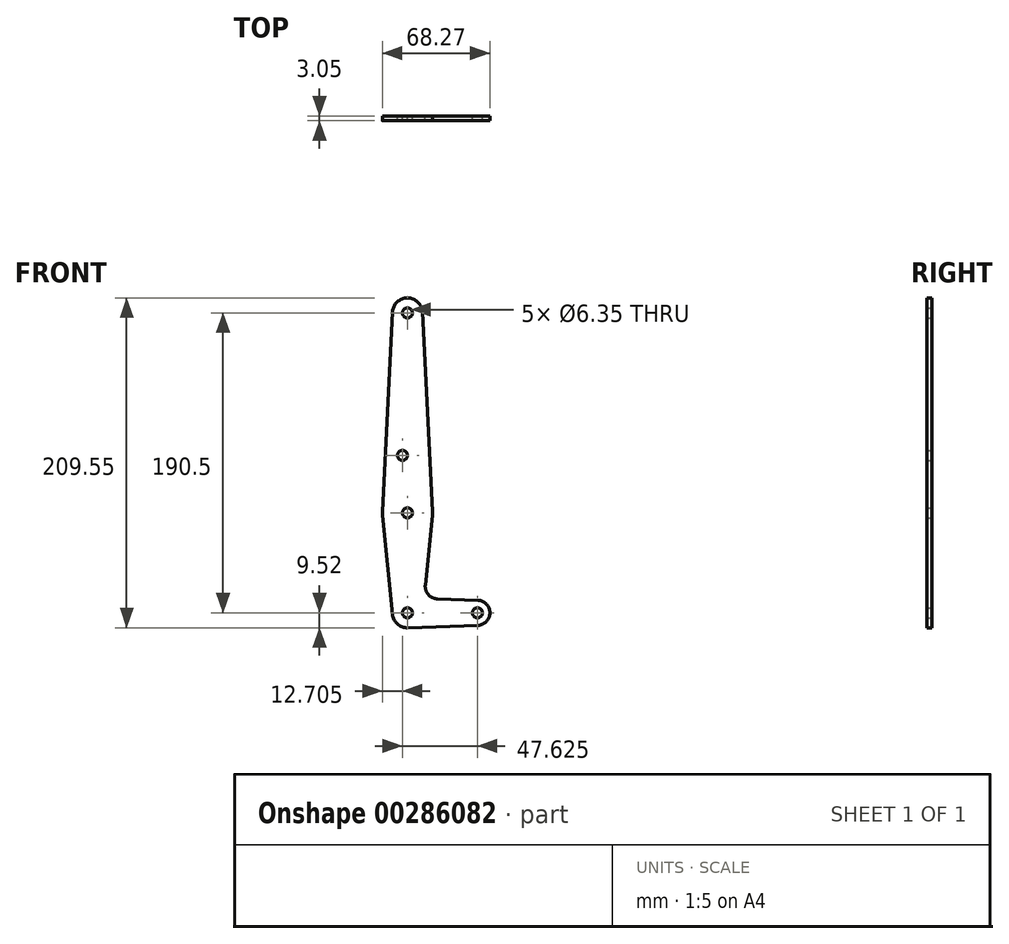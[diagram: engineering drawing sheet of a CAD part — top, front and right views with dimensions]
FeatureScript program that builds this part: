
annotation { "Feature Type Name" : "Feature", "Feature Type Description" : "" }
export const myFeature = defineFeature(function(context is Context, id is Id, definition is map)
    precondition{}
    {
        {
            var Q0;
            Q0=qCreatedBy(makeId("Front.planeOp"),FACE);
            var sketch = newSketch(context, id + "F0", { "sketchPlane" : qUnion([Q0])});
            skCircle(sketch, "E0", {"center": v(0, 0) * mm, "radius": 9.53 * mm});
            skCircle(sketch, "E1", {"center": v(0, 63.5) * mm, "radius": 15.88 * mm});
            skCircle(sketch, "E2", {"center": v(0, 190.5) * mm, "radius": 9.53 * mm});
            skLineSegment(sketch, "E3", {"start": v(0, 0) * mm, "end": v(44.45, 0) * mm, "construction": true});
            skCircle(sketch, "E4", {"center": v(44.45, 0) * mm, "radius": 7.94 * mm});
            skLineSegment(sketch, "E5", {"start": v(0, 190.5) * mm, "end": v(0, 0) * mm, "construction": true});
            skLineSegment(sketch, "E6", {"start": v(9.51, 190.98) * mm, "end": v(15.86, 64.3) * mm});
            skLineSegment(sketch, "E7", {"start": v(18.97, 8.85) * mm, "end": v(44.73, 7.93) * mm});
            skLineSegment(sketch, "E8", {"start": v(-9.51, 190.98) * mm, "end": v(-15.86, 64.3) * mm});
            skLineSegment(sketch, "E9", {"start": v(-15.8, 61.91) * mm, "end": v(-9.48, -0.95) * mm});
            skLineSegment(sketch, "E10", {"start": v(15.8, 61.91) * mm, "end": v(11.34, 17.6) * mm});
            skLineSegment(sketch, "E11", {"start": v(0.34, -9.52) * mm, "end": v(44.73, -7.93) * mm});
            skCircle(sketch, "E12", {"center": v(0, 190.5) * mm, "radius": 3.18 * mm});
            skCircle(sketch, "E13", {"center": v(0, 63.5) * mm, "radius": 3.18 * mm});
            skCircle(sketch, "E14", {"center": v(0, 0) * mm, "radius": 3.18 * mm});
            skCircle(sketch, "E15", {"center": v(44.45, 0) * mm, "radius": 3.18 * mm});
            skCircle(sketch, "E16", {"center": v(-3.17, 100.03) * mm, "radius": 3.18 * mm});
            skArc(sketch, "E17.filletArc", {"start": v(11.34, 17.6) * mm, "mid": v(13.26, 11.57) * mm, "end": v(18.97, 8.85) * mm});
            skSolve(sketch);
        }
        {
            var Q0;
            Q0=makeQuery(id+"F0.imprint","IMPRINT",FACE,{"disambiguationData":[TD([[makeQuery(id+"F0.imprint","IMPRINT",EDGE,{"derivedFrom":sQuery(id+"F0.wireOp",EDGE,"E12")}),-1.0]])]});
            var Q1;
            {var subQ0=sQuery(id+"F0.wireOp",EDGE,"E6");Q1=makeQuery(id+"F0.imprint","IMPRINT",FACE,{"disambiguationData":[TD([[makeQuery(id+"F0.imprint","IMPRINT",EDGE,{"derivedFrom":subQ0}),-1.0]])]});}
            var Q2;
            Q2=makeQuery(id+"F0.imprint","IMPRINT",FACE,{"disambiguationData":[TD([[makeQuery(id+"F0.imprint","IMPRINT",EDGE,{"derivedFrom":sQuery(id+"F0.wireOp",EDGE,"E13")}),-1.0]])]});
            var Q3;
            {var subQ0=sQuery(id+"F0.wireOp",EDGE,"E7");Q3=makeQuery(id+"F0.imprint","IMPRINT",FACE,{"disambiguationData":[TD([[makeQuery(id+"F0.imprint","IMPRINT",EDGE,{"derivedFrom":subQ0}),-1.0]])]});}
            var Q4;
            Q4=makeQuery(id+"F0.imprint","IMPRINT",FACE,{"disambiguationData":[TD([[makeQuery(id+"F0.imprint","IMPRINT",EDGE,{"derivedFrom":sQuery(id+"F0.wireOp",EDGE,"E14")}),-1.0]])]});
            var Q5;
            Q5=makeQuery(id+"F0.imprint","IMPRINT",FACE,{"disambiguationData":[TD([[makeQuery(id+"F0.imprint","IMPRINT",EDGE,{"derivedFrom":sQuery(id+"F0.wireOp",EDGE,"E15")}),-1.0]])]});
            extrude(context, id + "F1", {"entities" : qUnion([Q0, Q1, Q2, Q3, Q4, Q5]), "depth" : 3.05 * mm});
        }
    });
